MODEL slx_12b81e2f7ffb
CONFIG AbsTol = auto
CONFIG FixedStep = 0.01
CONFIG MaxStep = auto
CONFIG MinStep = auto
CONFIG RelTol = 1e-3
CONFIG SampleTimeConstraint = Unconstrained
CONFIG Solver = ode3
CONFIG SolverMode = Auto
CONFIG SolverName = ode3
CONFIG StartTime = 0.0
CONFIG StopTime = 50
BLOCK [SubSystem] DKM+Posture
  Ports = [2, 4]
  RequestExecContextInheritance = off
BLOCK [Fcn] DKM+Posture/Fcn
  Expr = sin(u)
BLOCK [Fcn] DKM+Posture/Fcn1
  Expr = 0.3*u(1)*cos(u(2))*cos(u(3))
BLOCK [Fcn] DKM+Posture/Fcn2
  Expr = 0.3*u(1)*cos(u(2))*sin(u(3))
BLOCK [Fcn] DKM+Posture/Fcn3
  Expr = u(1)*cos(u(3))+u(2)*sin(u(3))
BLOCK [Fcn] DKM+Posture/Fcn4
  Expr = -u(1)*sin(u(3))+u(2)*cos(u(3))
BLOCK [Fcn] DKM+Posture/Fcn5
  Expr = u(1)+0.3*cos(u(2))
BLOCK [Fcn] DKM+Posture/Fcn6
  Expr = u(1)+0.3*sin(u(2))
BLOCK [Integrator] DKM+Posture/Integrator
  Ports = [1, 1]
BLOCK [Integrator] DKM+Posture/Integrator1
  InitialCondition = 2.3
  Ports = [1, 1]
BLOCK [Integrator] DKM+Posture/Integrator2
  Ports = [1, 1]
BLOCK [Integrator] DKM+Posture/Integrator3
  InitialCondition = pi
  Ports = [1, 1]
BLOCK [Mux] DKM+Posture/Mux
  DisplayOption = bar
  Inputs = 3
  Ports = [3, 1]
BLOCK [Mux] DKM+Posture/Mux1
  DisplayOption = bar
  Inputs = 3
  Ports = [3, 1]
BLOCK [Mux] DKM+Posture/Mux2
  DisplayOption = bar
  Inputs = 3
  Ports = [3, 1]
BLOCK [Mux] DKM+Posture/Mux4
  DisplayOption = bar
  Inputs = 2
  Ports = [2, 1]
BLOCK [Mux] DKM+Posture/Mux5
  DisplayOption = bar
  Inputs = 2
  Ports = [2, 1]
BLOCK [Product] DKM+Posture/Product
  InputSameDT = off
  OutDataTypeStr = Inherit: Inherit via internal rule
  Ports = [2, 1]
  RndMeth = Floor
  SaturateOnIntegerOverflow = off
BLOCK [Sum] DKM+Posture/Sum
  IconShape = round
  InputSameDT = off
  Inputs = |++
  OutDataTypeStr = Inherit: Inherit via internal rule
  Ports = [2, 1]
  SaturateOnIntegerOverflow = off
BLOCK [ToWorkspace] DKM+Posture/To Workspace
  FixptAsFi = on
  MaxDataPoints = inf
  Ports = [1]
  SampleTime = -1
  Save2DSignal = 3-D array (concatenate along third dimension)
  VariableName = output
BLOCK [Inport] DKM+Posture/V
  IconDisplay = Port number
BLOCK [Reference] DKM+Posture/XY Graph  REF=simulink/Sinks/XY Graph
  Ports = [2]
  SourceBlock = simulink/Sinks/XY Graph
  SourceType = XY scope.
  st = -1
  xmax = 2
  xmin = -2
  ymax = 2
  ymin = -2
BLOCK [Outport] DKM+Posture/beta
  IconDisplay = Port number
  Port = 4
BLOCK [Inport] DKM+Posture/omega
  IconDisplay = Port number
  Port = 2
BLOCK [Outport] DKM+Posture/psi
  IconDisplay = Port number
  Port = 3
BLOCK [Outport] DKM+Posture/x
  IconDisplay = Port number
BLOCK [Outport] DKM+Posture/y
  IconDisplay = Port number
  Port = 2
BLOCK [SubSystem] Lyapunov Based Controller
  Ports = [1, 2]
  RequestExecContextInheritance = off
BLOCK [Demux] Lyapunov Based Controller/Demux
  DisplayOption = bar
  Outputs = 2
  Ports = [1, 2]
BLOCK [Inport] Lyapunov Based Controller/Errors & Other Inputs
  IconDisplay = Port number
BLOCK [MATLABFcn] Lyapunov Based Controller/Interpreted MATLAB Function
  MATLABFcn = lyapu(u)
  Ports = [1, 1]
BLOCK [Outport] Lyapunov Based Controller/Omega
  IconDisplay = Port number
  Port = 2
BLOCK [Outport] Lyapunov Based Controller/V
  IconDisplay = Port number
BLOCK [Mux] Mux1
  DisplayOption = bar
  Inputs = 7
  Ports = [7, 1]
BLOCK [SubSystem] Reference Trajectory Generator
  Ports = [1, 6]
  RequestExecContextInheritance = off
BLOCK [Constant] Reference Trajectory Generator/Angular velocity Desired
  Value = 0.5
BLOCK [Product] Reference Trajectory Generator/Divide
  InputSameDT = off
  Inputs = */
  OutDataTypeStr = Inherit: Inherit via internal rule
  Ports = [2, 1]
  RndMeth = Floor
  SaturateOnIntegerOverflow = off
BLOCK [Fcn] Reference Trajectory Generator/Fcn
  Expr = u(1)*cos(u(2))
BLOCK [Fcn] Reference Trajectory Generator/Fcn1
  Expr = u(1)*sin(u(2))
BLOCK [Fcn] Reference Trajectory Generator/Fcn5
  Expr = u(1)*cos(u(3))+u(2)*sin(u(3))
BLOCK [Fcn] Reference Trajectory Generator/Fcn6
  Expr = -u(1)*sin(u(3))+u(2)*cos(u(3))
BLOCK [Integrator] Reference Trajectory Generator/Integrator
  Ports = [1, 1]
BLOCK [Mux] Reference Trajectory Generator/Mux
  DisplayOption = bar
  Inputs = 2
  Ports = [2, 1]
BLOCK [Mux] Reference Trajectory Generator/Mux1
  DisplayOption = bar
  Inputs = 3
  Ports = [3, 1]
BLOCK [Mux] Reference Trajectory Generator/Mux3
  DisplayOption = bar
  Inputs = 3
  Ports = [3, 1]
BLOCK [Product] Reference Trajectory Generator/Product
  InputSameDT = off
  OutDataTypeStr = Inherit: Inherit via internal rule
  Ports = [2, 1]
  RndMeth = Floor
  SaturateOnIntegerOverflow = off
BLOCK [Constant] Reference Trajectory Generator/Radius
  Value = 2
BLOCK [Constant] Reference Trajectory Generator/Required Steering Angle
  Value = 0.1506
BLOCK [Constant] Reference Trajectory Generator/Steer velocity
  Value = 0
BLOCK [Sum] Reference Trajectory Generator/Sum
  IconShape = round
  InputSameDT = off
  Inputs = |++
  OutDataTypeStr = Inherit: Inherit via internal rule
  Ports = [2, 1]
  SaturateOnIntegerOverflow = off
BLOCK [Reference] Reference Trajectory Generator/XY Graph  REF=simulink/Sinks/XY Graph
  Ports = [2]
  SourceBlock = simulink/Sinks/XY Graph
  SourceType = XY scope.
  st = -1
  xmax = 2
  xmin = -2
  ymax = 2
  ymin = -2
BLOCK [Outport] Reference Trajectory Generator/betaR
  IconDisplay = Port number
  Port = 6
BLOCK [Constant] Reference Trajectory Generator/offset
  Value = pi/2
BLOCK [Inport] Reference Trajectory Generator/psi
  IconDisplay = Port number
BLOCK [Outport] Reference Trajectory Generator/psiR
  IconDisplay = Port number
  Port = 3
BLOCK [Outport] Reference Trajectory Generator/vR
  IconDisplay = Port number
  Port = 4
BLOCK [Constant] Reference Trajectory Generator/velocity1
  Value = 0.3*cos(0.1506)
BLOCK [Outport] Reference Trajectory Generator/wR
  IconDisplay = Port number
  Port = 5
BLOCK [Outport] Reference Trajectory Generator/xR
  IconDisplay = Port number
BLOCK [Outport] Reference Trajectory Generator/yR
  IconDisplay = Port number
  Port = 2
BLOCK [Scope] Scope
  DataFormat = StructureWithTime
  Floating = off
  LimitDataPoints = off
  NumInputPorts = 1
  Ports = [1]
  YMax = 2.72991
  YMin = -4.74777
BLOCK [Scope] Scope1
  DataFormat = StructureWithTime
  Floating = off
  LimitDataPoints = off
  NumInputPorts = 1
  Ports = [1]
  SaveName = ScopeData1
  YMax = 4.33795
  YMin = 0.16375
BLOCK [Scope] Scope2
  DataFormat = StructureWithTime
  Floating = off
  LimitDataPoints = off
  NumInputPorts = 1
  Ports = [1]
  SaveName = ScopeData2
  YMax = -1.21529
  YMin = -2.7208
BLOCK [Sum] Sum
  IconShape = round
  InputSameDT = off
  Inputs = |+-
  OutDataTypeStr = Inherit: Inherit via internal rule
  Ports = [2, 1]
  SaturateOnIntegerOverflow = off
BLOCK [Sum] Sum1
  IconShape = round
  InputSameDT = off
  Inputs = |+-
  OutDataTypeStr = Inherit: Inherit via internal rule
  Ports = [2, 1]
  SaturateOnIntegerOverflow = off
BLOCK [Sum] Sum2
  IconShape = round
  InputSameDT = off
  Inputs = |+-
  OutDataTypeStr = Inherit: Inherit via internal rule
  Ports = [2, 1]
  SaturateOnIntegerOverflow = off
BLOCK [Display] thetaE
  Decimation = 1
  Ports = [1]
BLOCK [Display] xError
  Decimation = 1
  Ports = [1]
BLOCK [Display] yError
  Decimation = 1
  Ports = [1]
LINE DKM+Posture/Fcn1:1 -> DKM+Posture/Integrator1:1
LINE DKM+Posture/Fcn2:1 -> DKM+Posture/Integrator2:1
LINE DKM+Posture/Fcn3:1 -> DKM+Posture/x:1
LINE DKM+Posture/Fcn4:1 -> DKM+Posture/y:1
LINE DKM+Posture/Fcn5:1 -> DKM+Posture/Mux1:1
LINE DKM+Posture/Fcn5:1 -> DKM+Posture/Mux2:1
LINE DKM+Posture/Fcn5:1 -> DKM+Posture/XY Graph:1
LINE DKM+Posture/Fcn6:1 -> DKM+Posture/Mux1:2
LINE DKM+Posture/Fcn6:1 -> DKM+Posture/Mux2:2
LINE DKM+Posture/Fcn6:1 -> DKM+Posture/XY Graph:2
LINE DKM+Posture/Fcn:1 -> DKM+Posture/Product:2
LINE DKM+Posture/Integrator1:1 -> DKM+Posture/Mux4:1
LINE DKM+Posture/Integrator2:1 -> DKM+Posture/Mux5:1
LINE DKM+Posture/Integrator3:1 -> DKM+Posture/Mux4:2
LINE DKM+Posture/Integrator3:1 -> DKM+Posture/Mux5:2
LINE DKM+Posture/Integrator3:1 -> DKM+Posture/Mux:3
LINE DKM+Posture/Integrator3:1 -> DKM+Posture/Sum:1
LINE DKM+Posture/Integrator:1 -> DKM+Posture/Fcn:1
LINE DKM+Posture/Integrator:1 -> DKM+Posture/Mux:2
LINE DKM+Posture/Integrator:1 -> DKM+Posture/Sum:2
LINE DKM+Posture/Integrator:1 -> DKM+Posture/beta:1
LINE DKM+Posture/Mux1:1 -> DKM+Posture/Fcn3:1
LINE DKM+Posture/Mux1:1 -> DKM+Posture/Fcn4:1
LINE DKM+Posture/Mux2:1 -> DKM+Posture/To Workspace:1
LINE DKM+Posture/Mux4:1 -> DKM+Posture/Fcn5:1
LINE DKM+Posture/Mux5:1 -> DKM+Posture/Fcn6:1
LINE DKM+Posture/Mux:1 -> DKM+Posture/Fcn1:1
LINE DKM+Posture/Mux:1 -> DKM+Posture/Fcn2:1
LINE DKM+Posture/Product:1 -> DKM+Posture/Integrator3:1
LINE DKM+Posture/Sum:1 -> DKM+Posture/Mux1:3
LINE DKM+Posture/Sum:1 -> DKM+Posture/Mux2:3
LINE DKM+Posture/Sum:1 -> DKM+Posture/psi:1
LINE DKM+Posture/V:1 -> DKM+Posture/Mux:1
LINE DKM+Posture/V:1 -> DKM+Posture/Product:1
LINE DKM+Posture/omega:1 -> DKM+Posture/Integrator:1
LINE DKM+Posture:1 -> Sum:2
LINE DKM+Posture:2 -> Sum1:2
LINE DKM+Posture:3 -> Reference Trajectory Generator:1
LINE DKM+Posture:3 -> Sum2:2
LINE DKM+Posture:4 -> Mux1:7
LINE Lyapunov Based Controller/Demux:1 -> Lyapunov Based Controller/V:1
LINE Lyapunov Based Controller/Demux:2 -> Lyapunov Based Controller/Omega:1
LINE Lyapunov Based Controller/Errors & Other Inputs:1 -> Lyapunov Based Controller/Interpreted MATLAB Function:1
LINE Lyapunov Based Controller/Interpreted MATLAB Function:1 -> Lyapunov Based Controller/Demux:1
LINE Lyapunov Based Controller:1 -> DKM+Posture:1
LINE Lyapunov Based Controller:2 -> DKM+Posture:2
LINE Mux1:1 -> Lyapunov Based Controller:1
LINE Reference Trajectory Generator/Angular velocity Desired:1 -> Reference Trajectory Generator/Integrator:1
LINE Reference Trajectory Generator/Angular velocity Desired:1 -> Reference Trajectory Generator/Product:2
LINE Reference Trajectory Generator/Divide:1 -> Reference Trajectory Generator/vR:1
LINE Reference Trajectory Generator/Fcn1:1 -> Reference Trajectory Generator/Mux1:2
LINE Reference Trajectory Generator/Fcn1:1 -> Reference Trajectory Generator/Mux3:2
LINE Reference Trajectory Generator/Fcn1:1 -> Reference Trajectory Generator/XY Graph:2
LINE Reference Trajectory Generator/Fcn5:1 -> Reference Trajectory Generator/xR:1
LINE Reference Trajectory Generator/Fcn6:1 -> Reference Trajectory Generator/yR:1
LINE Reference Trajectory Generator/Fcn:1 -> Reference Trajectory Generator/Mux1:1
LINE Reference Trajectory Generator/Fcn:1 -> Reference Trajectory Generator/Mux3:1
LINE Reference Trajectory Generator/Fcn:1 -> Reference Trajectory Generator/XY Graph:1
LINE Reference Trajectory Generator/Integrator:1 -> Reference Trajectory Generator/Mux:2
LINE Reference Trajectory Generator/Integrator:1 -> Reference Trajectory Generator/Sum:1
LINE Reference Trajectory Generator/Mux3:1 -> Reference Trajectory Generator/Fcn5:1
LINE Reference Trajectory Generator/Mux3:1 -> Reference Trajectory Generator/Fcn6:1
LINE Reference Trajectory Generator/Mux:1 -> Reference Trajectory Generator/Fcn1:1
LINE Reference Trajectory Generator/Mux:1 -> Reference Trajectory Generator/Fcn:1
LINE Reference Trajectory Generator/Product:1 -> Reference Trajectory Generator/Divide:1
LINE Reference Trajectory Generator/Radius:1 -> Reference Trajectory Generator/Mux:1
LINE Reference Trajectory Generator/Radius:1 -> Reference Trajectory Generator/Product:1
LINE Reference Trajectory Generator/Required Steering Angle:1 -> Reference Trajectory Generator/betaR:1
LINE Reference Trajectory Generator/Steer velocity:1 -> Reference Trajectory Generator/wR:1
LINE Reference Trajectory Generator/Sum:1 -> Reference Trajectory Generator/psiR:1
LINE Reference Trajectory Generator/offset:1 -> Reference Trajectory Generator/Sum:2
LINE Reference Trajectory Generator/psi:1 -> Reference Trajectory Generator/Mux3:3
LINE Reference Trajectory Generator/velocity1:1 -> Reference Trajectory Generator/Divide:2
LINE Reference Trajectory Generator:1 -> Sum:1
LINE Reference Trajectory Generator:2 -> Sum1:1
LINE Reference Trajectory Generator:3 -> Sum2:1
LINE Reference Trajectory Generator:4 -> Mux1:4
LINE Reference Trajectory Generator:5 -> Mux1:5
LINE Reference Trajectory Generator:6 -> Mux1:6
LINE Sum1:1 -> Mux1:2
LINE Sum1:1 -> Scope1:1
LINE Sum1:1 -> yError:1
LINE Sum2:1 -> Mux1:3
LINE Sum2:1 -> Scope2:1
LINE Sum2:1 -> thetaE:1
LINE Sum:1 -> Mux1:1
LINE Sum:1 -> Scope:1
LINE Sum:1 -> xError:1
